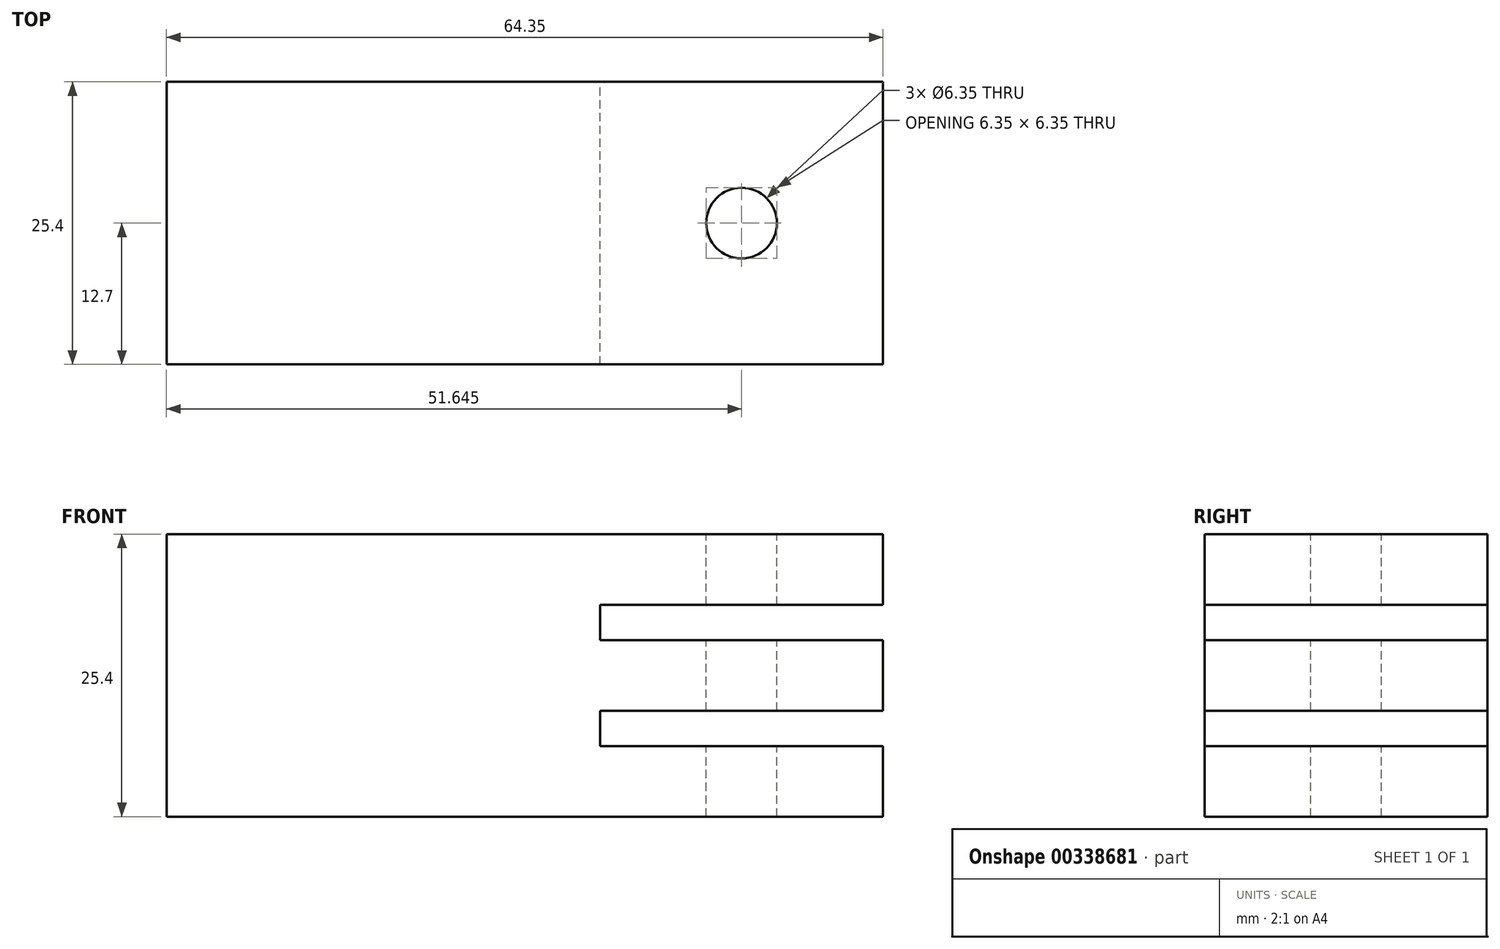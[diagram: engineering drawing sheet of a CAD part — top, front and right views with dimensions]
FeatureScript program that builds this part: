
annotation { "Feature Type Name" : "Feature", "Feature Type Description" : "" }
export const myFeature = defineFeature(function(context is Context, id is Id, definition is map)
    precondition{}
    {
        {
            var Q0;
            Q0=qCreatedBy(makeId("Front.planeOp"),FACE);
            var sketch = newSketch(context, id + "F0", { "sketchPlane" : qUnion([Q0])});
            skLineSegment(sketch, "E0.bottom", {"start": v(-48.06, 9.78) * mm, "end": v(16.29, 9.78) * mm});
            skLineSegment(sketch, "E0.top", {"start": v(-48.06, -15.62) * mm, "end": v(16.29, -15.62) * mm});
            skLineSegment(sketch, "E0.left", {"start": v(-48.06, 9.78) * mm, "end": v(-48.06, -15.62) * mm});
            skLineSegment(sketch, "E0.right", {"start": v(16.29, 9.78) * mm, "end": v(16.29, 3.43) * mm});
            skLineSegment(sketch, "E1", {"start": v(16.29, 3.43) * mm, "end": v(-9.11, 3.43) * mm});
            skLineSegment(sketch, "E2", {"start": v(-9.11, 3.43) * mm, "end": v(-9.11, 0.26) * mm});
            skLineSegment(sketch, "E3", {"start": v(-9.11, 0.26) * mm, "end": v(16.29, 0.26) * mm});
            skLineSegment(sketch, "E4", {"start": v(16.29, 0.26) * mm, "end": v(16.29, -6.1) * mm});
            skLineSegment(sketch, "E5", {"start": v(16.29, -6.1) * mm, "end": v(-9.11, -6.1) * mm});
            skLineSegment(sketch, "E6", {"start": v(-9.11, -6.1) * mm, "end": v(-9.11, -9.27) * mm});
            skLineSegment(sketch, "E7", {"start": v(-9.11, -9.27) * mm, "end": v(16.29, -9.27) * mm});
            skLineSegment(sketch, "E8.trimOffspring", {"start": v(16.29, -9.27) * mm, "end": v(16.29, -15.62) * mm});
            skSolve(sketch);
        }
        {
            var Q0;
            Q0 = qSketchRegion(id + "F0", true);
            extrude(context, id + "F1", {"entities" : qUnion([Q0]), "depth" : 25.4 * mm});
        }
        {
            var Q0;
            Q0=makeQuery(id+"F1.opExtrude","SWEPT_FACE",FACE,{"disambiguationData":[OSD([sQuery(id+"F0.wireOp",EDGE,"E0.bottom")])]});
            var sketch = newSketch(context, id + "F2", { "sketchPlane" : qUnion([Q0])});
            skCircle(sketch, "E9", {"center": v(3.59, -12.7) * mm, "radius": 3.17 * mm});
            skSolve(sketch);
        }
        {
            var Q0;
            Q0 = qSketchRegion(id + "F2", true);
            extrude(context, id + "F3", {"entities" : qUnion([Q0]), "operationType" : NewBodyOperationType.REMOVE, "oppositeDirection" : true, "depth" : 38.1 * mm});
        }
    });
